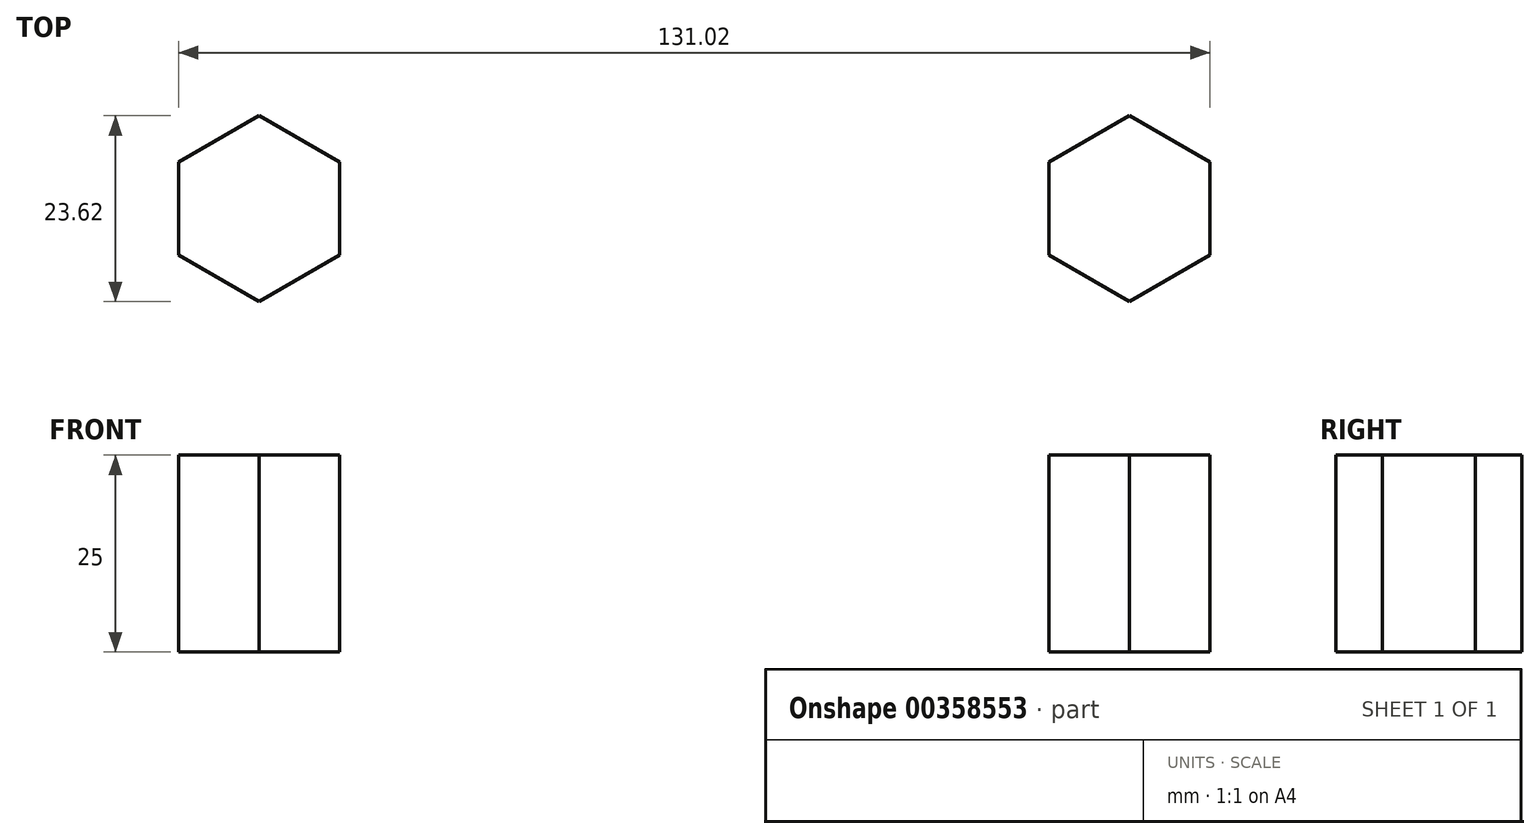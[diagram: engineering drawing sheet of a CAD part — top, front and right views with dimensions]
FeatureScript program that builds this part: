
annotation { "Feature Type Name" : "Feature", "Feature Type Description" : "" }
export const myFeature = defineFeature(function(context is Context, id is Id, definition is map)
    precondition{}
    {
        {
            var Q0;
            Q0=qCreatedBy(makeId("Top.planeOp"),FACE);
            var sketch = newSketch(context, id + "F0", { "sketchPlane" : qUnion([Q0])});
            skCircle(sketch, "E0.cCircle", {"center": v(-58.44, 0) * mm, "radius": 10.23 * mm, "construction": true});
            skLineSegment(sketch, "E0.0", {"start": v(-48.21, 5.9) * mm, "end": v(-48.21, -5.9) * mm});
            skLineSegment(sketch, "E0.1", {"start": v(-48.21, -5.9) * mm, "end": v(-58.44, -11.81) * mm});
            skLineSegment(sketch, "E0.2", {"start": v(-58.44, -11.81) * mm, "end": v(-68.67, -5.9) * mm});
            skLineSegment(sketch, "E0.3", {"start": v(-68.67, -5.9) * mm, "end": v(-68.67, 5.9) * mm});
            skLineSegment(sketch, "E0.4", {"start": v(-68.67, 5.9) * mm, "end": v(-58.44, 11.81) * mm});
            skLineSegment(sketch, "E0.5", {"start": v(-58.44, 11.81) * mm, "end": v(-48.21, 5.9) * mm});
            skPoint(sketch, "E0.0.midPoint", {"position": v(-48.21, 0) * mm});
            skCircle(sketch, "E1.cCircle", {"center": v(52.12, 0) * mm, "radius": 10.23 * mm, "construction": true});
            skLineSegment(sketch, "E1.0", {"start": v(62.35, 5.9) * mm, "end": v(62.35, -5.9) * mm});
            skLineSegment(sketch, "E1.1", {"start": v(62.35, -5.9) * mm, "end": v(52.12, -11.81) * mm});
            skLineSegment(sketch, "E1.2", {"start": v(52.12, -11.81) * mm, "end": v(41.9, -5.9) * mm});
            skLineSegment(sketch, "E1.3", {"start": v(41.9, -5.9) * mm, "end": v(41.9, 5.9) * mm});
            skLineSegment(sketch, "E1.4", {"start": v(41.9, 5.9) * mm, "end": v(52.12, 11.81) * mm});
            skLineSegment(sketch, "E1.5", {"start": v(52.12, 11.81) * mm, "end": v(62.35, 5.9) * mm});
            skPoint(sketch, "E1.0.midPoint", {"position": v(62.35, 0) * mm});
            skSolve(sketch);
        }
        {
            var Q0;
            Q0=makeQuery(id+"F0.imprint","IMPRINT",FACE,{"disambiguationData":[TD([[makeQuery(id+"F0.imprint","IMPRINT",EDGE,{"derivedFrom":sQuery(id+"F0.wireOp",EDGE,"E0.0")}),-1.0]])]});
            var Q1;
            Q1=makeQuery(id+"F0.imprint","IMPRINT",FACE,{"disambiguationData":[TD([[makeQuery(id+"F0.imprint","IMPRINT",EDGE,{"derivedFrom":sQuery(id+"F0.wireOp",EDGE,"E1.0")}),-1.0]])]});
            extrude(context, id + "F1", {"entities" : qUnion([Q0, Q1]), "depth" : 25 * mm});
        }
    });
